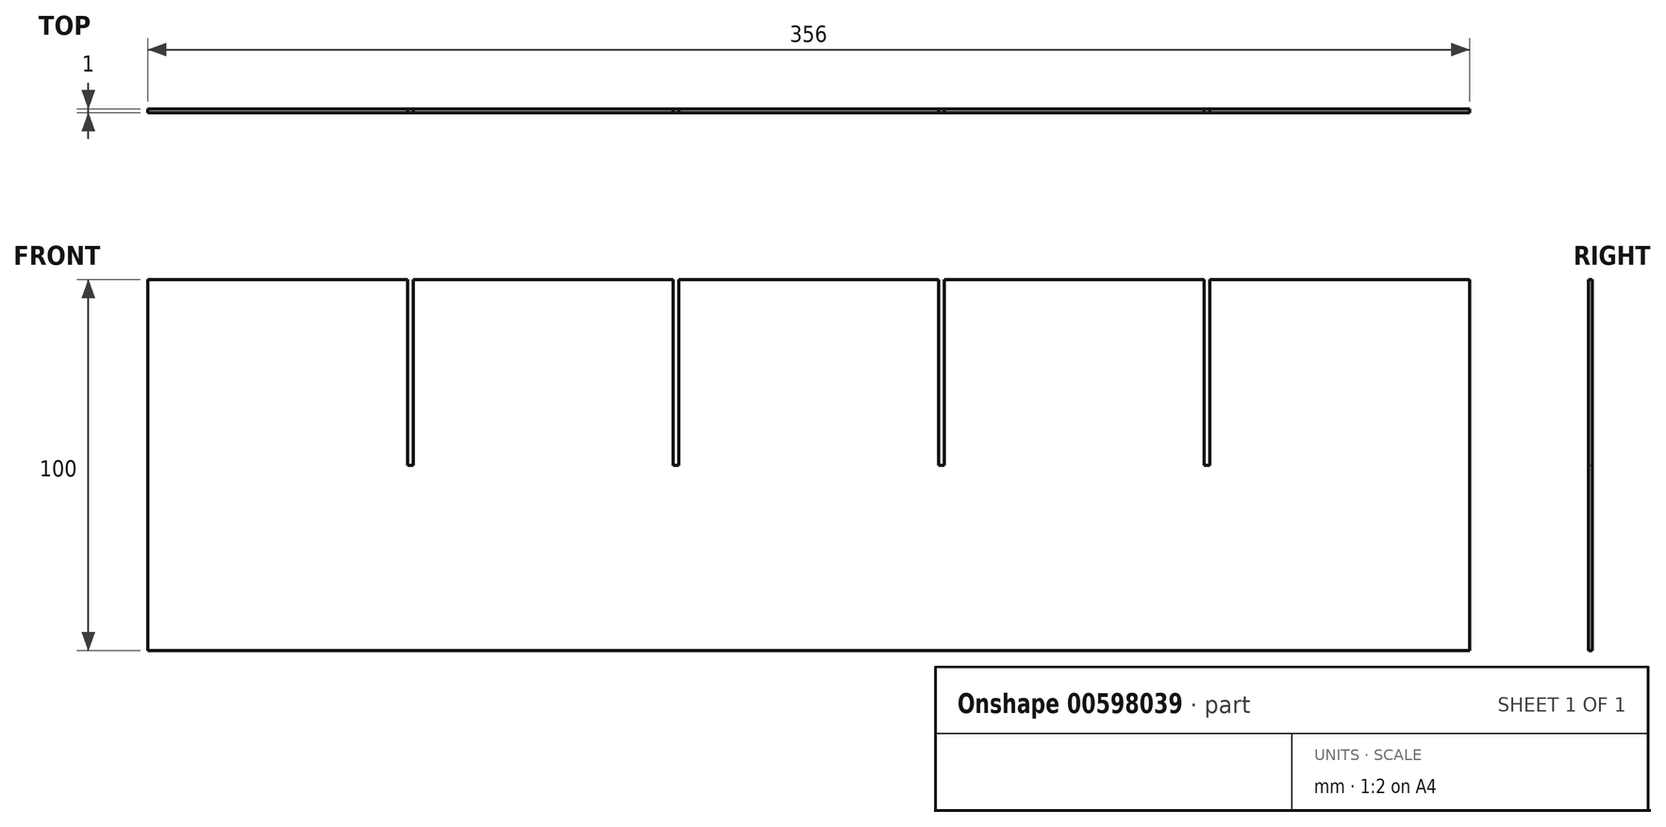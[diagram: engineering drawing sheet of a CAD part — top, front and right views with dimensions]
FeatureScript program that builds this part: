
annotation { "Feature Type Name" : "Feature", "Feature Type Description" : "" }
export const myFeature = defineFeature(function(context is Context, id is Id, definition is map)
    precondition{}
    {
        {
            var Q0;
            Q0=qCreatedBy(makeId("Front.planeOp"),FACE);
            var sketch = newSketch(context, id + "F0", { "sketchPlane" : qUnion([Q0])});
            skLineSegment(sketch, "E0", {"start": v(-106.93, -63.3) * mm, "end": v(-106.93, 36.7) * mm});
            skLineSegment(sketch, "E1", {"start": v(-106.93, 36.7) * mm, "end": v(-36.93, 36.7) * mm});
            skLineSegment(sketch, "E2", {"start": v(-36.93, 36.7) * mm, "end": v(-36.93, -13.3) * mm});
            skLineSegment(sketch, "E3", {"start": v(-36.93, -13.3) * mm, "end": v(-35.43, -13.3) * mm});
            skLineSegment(sketch, "E4", {"start": v(-35.43, -13.3) * mm, "end": v(-35.43, 36.7) * mm});
            skLineSegment(sketch, "E5", {"start": v(-35.43, 36.7) * mm, "end": v(34.57, 36.7) * mm});
            skLineSegment(sketch, "E6", {"start": v(34.57, 36.7) * mm, "end": v(34.57, -13.3) * mm});
            skLineSegment(sketch, "E7", {"start": v(34.57, -13.3) * mm, "end": v(36.07, -13.3) * mm});
            skLineSegment(sketch, "E8", {"start": v(36.07, -13.3) * mm, "end": v(36.07, 36.7) * mm});
            skLineSegment(sketch, "E9", {"start": v(36.07, 36.7) * mm, "end": v(106.07, 36.7) * mm});
            skLineSegment(sketch, "E10", {"start": v(106.07, 36.7) * mm, "end": v(106.07, -13.3) * mm});
            skLineSegment(sketch, "E11", {"start": v(106.07, -13.3) * mm, "end": v(107.57, -13.3) * mm});
            skLineSegment(sketch, "E12", {"start": v(107.57, -13.3) * mm, "end": v(107.57, 36.7) * mm});
            skLineSegment(sketch, "E13", {"start": v(107.57, 36.7) * mm, "end": v(177.57, 36.7) * mm});
            skLineSegment(sketch, "E14", {"start": v(177.57, 36.7) * mm, "end": v(177.57, -13.3) * mm});
            skLineSegment(sketch, "E15", {"start": v(177.57, -13.3) * mm, "end": v(179.07, -13.3) * mm});
            skLineSegment(sketch, "E16", {"start": v(179.07, -13.3) * mm, "end": v(179.07, 36.7) * mm});
            skLineSegment(sketch, "E17", {"start": v(179.07, 36.7) * mm, "end": v(249.07, 36.7) * mm});
            skLineSegment(sketch, "E18", {"start": v(249.07, 36.7) * mm, "end": v(249.07, -63.3) * mm});
            skLineSegment(sketch, "E19", {"start": v(249.07, -63.3) * mm, "end": v(-106.93, -63.3) * mm});
            skSolve(sketch);
        }
        {
            var Q0;
            Q0=makeQuery(id+"F0.imprint","IMPRINT",FACE,{"disambiguationData":[TD([[makeQuery(id+"F0.imprint","IMPRINT",EDGE,{"derivedFrom":sQuery(id+"F0.wireOp",EDGE,"E0")}),-1.0]])]});
            extrude(context, id + "F1", {"entities" : qUnion([Q0]), "depth" : 1 * mm, "offsetDistance" : 25 * mm});
        }
    });
